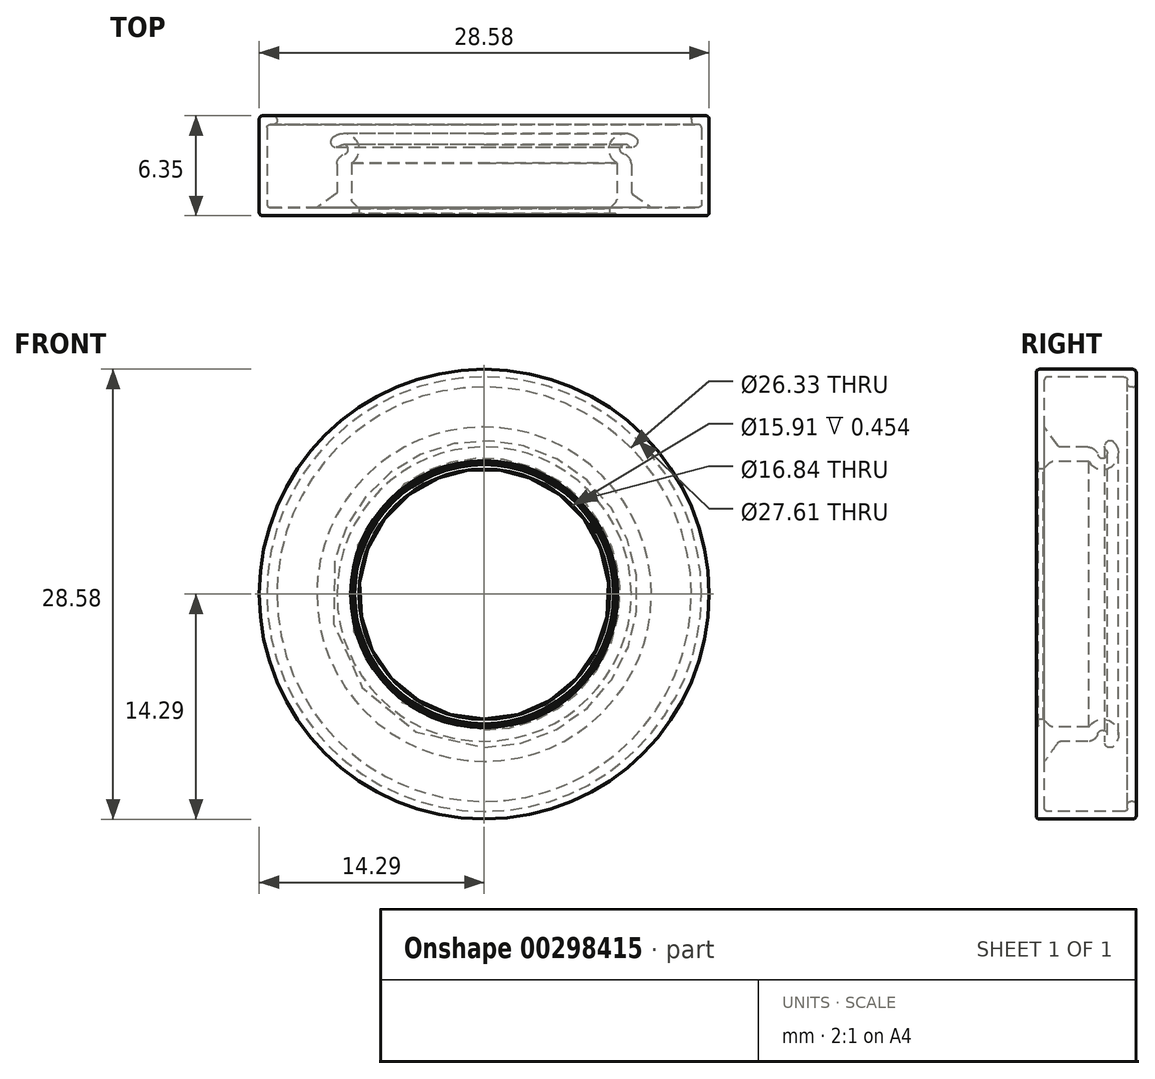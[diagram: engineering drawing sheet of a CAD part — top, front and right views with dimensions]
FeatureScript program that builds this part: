
annotation { "Feature Type Name" : "Feature", "Feature Type Description" : "" }
export const myFeature = defineFeature(function(context is Context, id is Id, definition is map)
    precondition{}
    {
        {
            var Q0;
            Q0=qCreatedBy(makeId("Top.planeOp"),FACE);
            var sketch = newSketch(context, id + "F0", { "sketchPlane" : qUnion([Q0])});
            skLineSegment(sketch, "E0", {"start": v(0, 0.46) * mm, "end": v(0, 7.99) * mm});
            skLineSegment(sketch, "E1", {"start": v(-13.16, 6.14) * mm, "end": v(-13.16, 6) * mm});
            skLineSegment(sketch, "E2", {"start": v(-13.37, 5.8) * mm, "end": v(-13.6, 5.8) * mm});
            skLineSegment(sketch, "E3", {"start": v(-13.8, 5.58) * mm, "end": v(-13.8, 0.74) * mm});
            skLineSegment(sketch, "E4", {"start": v(-13.6, 0.53) * mm, "end": v(-10.62, 0.53) * mm});
            skLineSegment(sketch, "E5", {"start": v(-10.62, 0.53) * mm, "end": v(-9.44, 1.37) * mm});
            skLineSegment(sketch, "E6", {"start": v(-9.35, 1.55) * mm, "end": v(-9.35, 3.29) * mm});
            skLineSegment(sketch, "E7", {"start": v(-13.37, 6.35) * mm, "end": v(-14.08, 6.35) * mm});
            skLineSegment(sketch, "E8", {"start": v(-14.29, 6.14) * mm, "end": v(-14.29, 0.2) * mm});
            skLineSegment(sketch, "E9", {"start": v(-14.08, 0) * mm, "end": v(-8.48, 0) * mm});
            skArc(sketch, "E10", {"start": v(-8.42, 3.35) * mm, "mid": v(-8.14, 4.82) * mm, "end": v(-9.64, 4.95) * mm});
            skArc(sketch, "E11", {"start": v(-8.87, 3.91) * mm, "mid": v(-8.68, 4.36) * mm, "end": v(-9.16, 4.44) * mm});
            skArc(sketch, "E12", {"start": v(-8.87, 3.91) * mm, "mid": v(-9.21, 3.68) * mm, "end": v(-9.35, 3.29) * mm});
            skArc(sketch, "E13", {"start": v(-9.64, 4.95) * mm, "mid": v(-9.65, 4.46) * mm, "end": v(-9.16, 4.44) * mm});
            skLineSegment(sketch, "E14", {"start": v(-7.95, 0) * mm, "end": v(-8.23, 0) * mm});
            skLineSegment(sketch, "E15", {"start": v(-8.23, 0) * mm, "end": v(-8.35, 0.15) * mm});
            skLineSegment(sketch, "E16", {"start": v(-8.35, 0.15) * mm, "end": v(-8.48, 0) * mm});
            skLineSegment(sketch, "E17", {"start": v(-7.95, 0) * mm, "end": v(-7.95, 0.45) * mm});
            skLineSegment(sketch, "E18", {"start": v(-7.95, 0.45) * mm, "end": v(-8.36, 0.88) * mm});
            skLineSegment(sketch, "E19", {"start": v(-8.42, 1.02) * mm, "end": v(-8.42, 3.35) * mm});
            skPoint(sketch, "E20.visualSharp", {"position": v(-13.8, 0.53) * mm});
            skArc(sketch, "E20.filletArc", {"start": v(-13.8, 0.74) * mm, "mid": v(-13.74, 0.59) * mm, "end": v(-13.6, 0.53) * mm});
            skPoint(sketch, "E21.visualSharp", {"position": v(-14.29, 0) * mm});
            skArc(sketch, "E21.filletArc", {"start": v(-14.29, 0.2) * mm, "mid": v(-14.23, 0.06) * mm, "end": v(-14.08, 0) * mm});
            skPoint(sketch, "E22.visualSharp", {"position": v(-14.29, 6.35) * mm});
            skArc(sketch, "E22.filletArc", {"start": v(-14.08, 6.35) * mm, "mid": v(-14.23, 6.29) * mm, "end": v(-14.29, 6.14) * mm});
            skPoint(sketch, "E23.visualSharp", {"position": v(-13.16, 6.35) * mm});
            skArc(sketch, "E23.filletArc", {"start": v(-13.16, 6.14) * mm, "mid": v(-13.23, 6.29) * mm, "end": v(-13.37, 6.35) * mm});
            skPoint(sketch, "E24.visualSharp", {"position": v(-13.8, 5.8) * mm});
            skArc(sketch, "E24.filletArc", {"start": v(-13.6, 5.8) * mm, "mid": v(-13.74, 5.73) * mm, "end": v(-13.8, 5.58) * mm});
            skPoint(sketch, "E25.visualSharp", {"position": v(-13.16, 5.8) * mm});
            skArc(sketch, "E25.filletArc", {"start": v(-13.37, 5.8) * mm, "mid": v(-13.23, 5.86) * mm, "end": v(-13.16, 6) * mm});
            skPoint(sketch, "E26.visualSharp", {"position": v(-9.35, 1.44) * mm});
            skArc(sketch, "E26.filletArc", {"start": v(-9.44, 1.37) * mm, "mid": v(-9.37, 1.45) * mm, "end": v(-9.35, 1.55) * mm});
            skPoint(sketch, "E27.visualSharp", {"position": v(-8.42, 0.94) * mm});
            skArc(sketch, "E27.filletArc", {"start": v(-8.42, 1.02) * mm, "mid": v(-8.4, 0.94) * mm, "end": v(-8.36, 0.88) * mm});
            skSolve(sketch);
        }
        {
            var Q0;
            Q0=makeQuery(id+"F0.imprint","IMPRINT",FACE,{"disambiguationData":[TD([[makeQuery(id+"F0.imprint","IMPRINT",EDGE,{"derivedFrom":sQuery(id+"F0.wireOp",EDGE,"E1")}),-1.0]])]});
            var Q1;
            Q1=sQuery(id+"F0.wireOp",EDGE,"E0");
            revolve(context, id + "F1", {"entities" : qUnion([Q0]), "axis" : qUnion([Q1]), "revolveType" : RevolveType.FULL});
        }
    });
